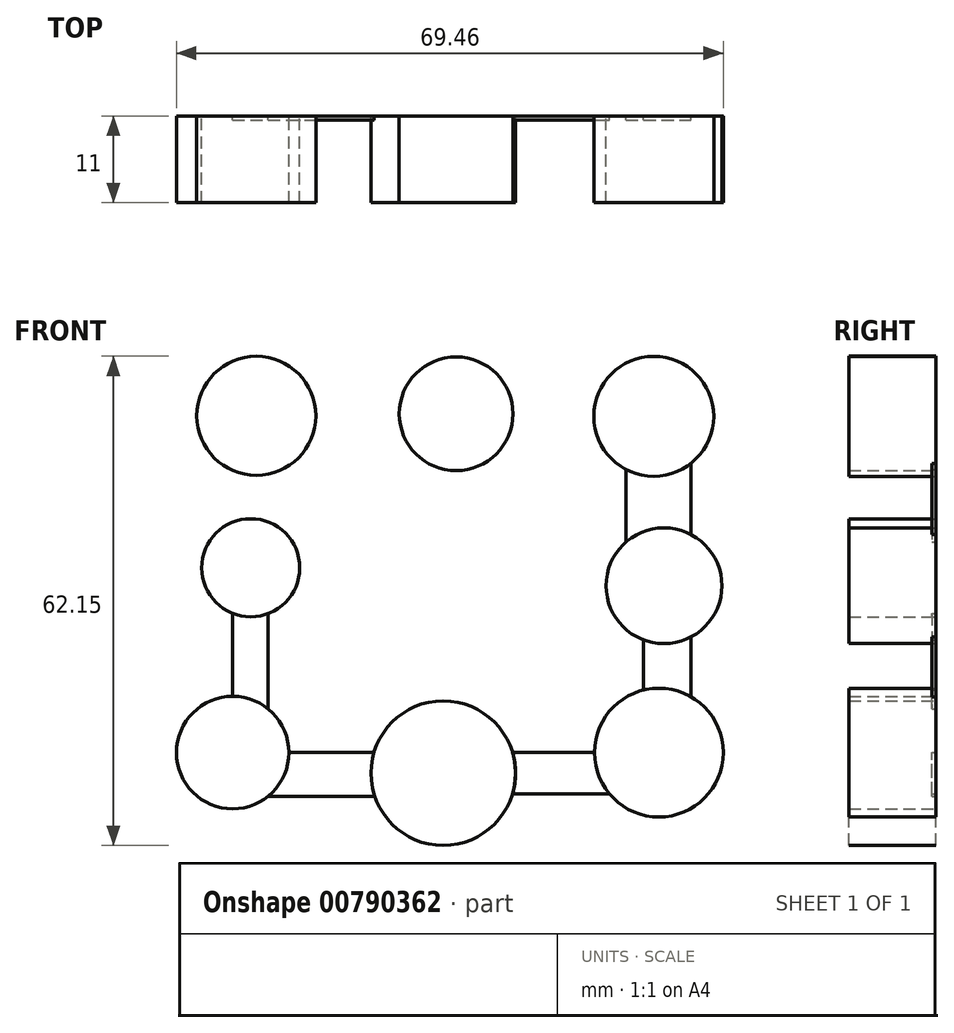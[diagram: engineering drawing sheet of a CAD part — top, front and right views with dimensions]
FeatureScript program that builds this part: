
annotation { "Feature Type Name" : "Feature", "Feature Type Description" : "" }
export const myFeature = defineFeature(function(context is Context, id is Id, definition is map)
    precondition{}
    {
        {
            var Q0;
            Q0=qCreatedBy(makeId("Front.planeOp"),FACE);
            var sketch = newSketch(context, id + "F0", { "sketchPlane" : qUnion([Q0])});
            skCircle(sketch, "E0", {"center": v(-55.2, 42.79) * mm, "radius": 7.57 * mm});
            skLineSegment(sketch, "E1", {"start": v(-48.07, 45.33) * mm, "end": v(-36.68, 45.33) * mm});
            skLineSegment(sketch, "E2", {"start": v(-48.08, 40.23) * mm, "end": v(-37, 40.23) * mm});
            skCircle(sketch, "E3", {"center": v(-29.83, 43.04) * mm, "radius": 7.22 * mm});
            skLineSegment(sketch, "E4", {"start": v(-23.46, 46.43) * mm, "end": v(-11.57, 46.43) * mm});
            skLineSegment(sketch, "E5", {"start": v(-23.31, 39.94) * mm, "end": v(-11.9, 39.94) * mm});
            skCircle(sketch, "E6", {"center": v(-4.72, 42.72) * mm, "radius": 7.61 * mm});
            skLineSegment(sketch, "E7", {"start": v(-58.22, 35.84) * mm, "end": v(-58.22, 29.35) * mm});
            skLineSegment(sketch, "E8", {"start": v(-52.3, 35.8) * mm, "end": v(-52.3, 28.7) * mm});
            skCircle(sketch, "E9", {"center": v(-55.92, 23.48) * mm, "radius": 6.23 * mm});
            skLineSegment(sketch, "E10", {"start": v(-58.22, 17.69) * mm, "end": v(-58.22, 6.2) * mm});
            skLineSegment(sketch, "E11", {"start": v(-53.72, 17.65) * mm, "end": v(-53.72, 5.54) * mm});
            skCircle(sketch, "E12", {"center": v(-58.22, 0) * mm, "radius": 7.14 * mm});
            skPoint(sketch, "E12.centerSnap0", {"position": v(-58.22, 11.94) * mm});
            skLineSegment(sketch, "E13", {"start": v(-51.08, 0) * mm, "end": v(-40.27, 0) * mm});
            skLineSegment(sketch, "E14", {"start": v(-53.72, -5.54) * mm, "end": v(-38.97, -5.54) * mm});
            skPoint(sketch, "E14.startSnap0", {"position": v(-53.72, 11.6) * mm});
            skCircle(sketch, "E15", {"center": v(-31.47, -2.6) * mm, "radius": 9.18 * mm});
            skLineSegment(sketch, "E16", {"start": v(-8.26, 35.97) * mm, "end": v(-8.26, 26.74) * mm});
            skLineSegment(sketch, "E17", {"start": v(0, 36.75) * mm, "end": v(0, 26.74) * mm});
            skCircle(sketch, "E18", {"center": v(-3.42, 21.2) * mm, "radius": 7.36 * mm});
            skCircle(sketch, "E19", {"center": v(-4.08, 0) * mm, "radius": 8.18 * mm});
            skLineSegment(sketch, "E20", {"start": v(-6.04, 14.32) * mm, "end": v(-6.04, 7.94) * mm});
            skLineSegment(sketch, "E21", {"start": v(0, 14.69) * mm, "end": v(0, 7.1) * mm});
            skLineSegment(sketch, "E22", {"start": v(-22.66, 0) * mm, "end": v(-12.25, 0) * mm});
            skLineSegment(sketch, "E23", {"start": v(-22.66, -5.22) * mm, "end": v(-10.37, -5.22) * mm});
            skSolve(sketch);
        }
        {
            var Q0;
            Q0=makeQuery(id+"F0.imprint","IMPRINT",FACE,{"disambiguationData":[TD([[makeQuery(id+"F0.imprint","IMPRINT",EDGE,{"derivedFrom":sQuery(id+"F0.wireOp",EDGE,"E0")}),1.0]])]});
            extrude(context, id + "F1", {"entities" : qUnion([Q0]), "depth" : 11 * mm, "offsetDistance" : 25.4 * mm});
        }
        {
            var Q0;
            {var subQ0=sQuery(id+"F0.wireOp",EDGE,"E9");var subQ1=makeQuery(id+"F0.imprint","INTERSECT",VERTEX,{"derivedFrom":[subQ0,sQuery(id+"F0.wireOp",EDGE,"E10")]});Q0=makeQuery(id+"F0.imprint","IMPRINT",FACE,{"disambiguationData":[TD([[makeQuery(id+"F0.imprint","IMPRINT",EDGE,{"disambiguationData":[TD([[subQ1,-1.0]])],"derivedFrom":subQ0}),1.0]])]});}
            var Q1;
            {var subQ0=sQuery(id+"F0.wireOp",EDGE,"E12");var subQ1=makeQuery(id+"F0.imprint","INTERSECT",VERTEX,{"derivedFrom":[sQuery(id+"F0.wireOp",EDGE,"E11"),subQ0]});Q1=makeQuery(id+"F0.imprint","IMPRINT",FACE,{"disambiguationData":[TD([[makeQuery(id+"F0.imprint","IMPRINT",EDGE,{"disambiguationData":[TD([[subQ1,1.0]])],"derivedFrom":subQ0}),1.0]])]});}
            var Q2;
            {var subQ0=sQuery(id+"F0.wireOp",EDGE,"E15");var subQ1=makeQuery(id+"F0.imprint","INTERSECT",VERTEX,{"derivedFrom":[sQuery(id+"F0.wireOp",EDGE,"E13"),subQ0]});Q2=makeQuery(id+"F0.imprint","IMPRINT",FACE,{"disambiguationData":[TD([[makeQuery(id+"F0.imprint","IMPRINT",EDGE,{"disambiguationData":[TD([[subQ1,1.0]])],"derivedFrom":subQ0}),1.0]])]});}
            var Q3;
            {var subQ0=sQuery(id+"F0.wireOp",EDGE,"E19");var subQ1=makeQuery(id+"F0.imprint","INTERSECT",VERTEX,{"derivedFrom":[subQ0,sQuery(id+"F0.wireOp",EDGE,"E20")]});Q3=makeQuery(id+"F0.imprint","IMPRINT",FACE,{"disambiguationData":[TD([[makeQuery(id+"F0.imprint","IMPRINT",EDGE,{"disambiguationData":[TD([[subQ1,1.0]])],"derivedFrom":subQ0}),1.0]])]});}
            var Q4;
            {var subQ0=sQuery(id+"F0.wireOp",EDGE,"E18");var subQ1=makeQuery(id+"F0.imprint","INTERSECT",VERTEX,{"derivedFrom":[sQuery(id+"F0.wireOp",EDGE,"E16"),subQ0]});Q4=makeQuery(id+"F0.imprint","IMPRINT",FACE,{"disambiguationData":[TD([[makeQuery(id+"F0.imprint","IMPRINT",EDGE,{"disambiguationData":[TD([[subQ1,1.0]])],"derivedFrom":subQ0}),1.0]])]});}
            var Q5;
            {var subQ0=sQuery(id+"F0.wireOp",EDGE,"E6");var subQ1=makeQuery(id+"F0.imprint","INTERSECT",VERTEX,{"derivedFrom":[subQ0,sQuery(id+"F0.wireOp",EDGE,"E16")]});Q5=makeQuery(id+"F0.imprint","IMPRINT",FACE,{"disambiguationData":[TD([[makeQuery(id+"F0.imprint","IMPRINT",EDGE,{"disambiguationData":[TD([[subQ1,-1.0]])],"derivedFrom":subQ0}),1.0]])]});}
            var Q6;
            {var subQ0=sQuery(id+"F0.wireOp",EDGE,"E3");var subQ1=makeQuery(id+"F0.imprint","IMPRINT",VERTEX,{"disambiguationData":[OD(0.0)],"derivedFrom":subQ0});Q6=makeQuery(id+"F0.imprint","IMPRINT",FACE,{"disambiguationData":[TD([[makeQuery(id+"F0.imprint","IMPRINT",EDGE,{"disambiguationData":[TD([[subQ1,1.0]])],"derivedFrom":subQ0}),1.0]])]});}
            extrude(context, id + "F2", {"entities" : qUnion([Q0, Q1, Q2, Q3, Q4, Q5, Q6]), "depth" : 11 * mm, "offsetDistance" : 25 * mm});
        }
        {
            var Q0;
            {var subQ0=sQuery(id+"F0.wireOp",EDGE,"E13");Q0=makeQuery(id+"F0.imprint","IMPRINT",FACE,{"disambiguationData":[TD([[makeQuery(id+"F0.imprint","IMPRINT",EDGE,{"derivedFrom":subQ0}),-1.0]])]});}
            var Q1;
            {var subQ0=sQuery(id+"F0.wireOp",EDGE,"E22");Q1=makeQuery(id+"F0.imprint","IMPRINT",FACE,{"disambiguationData":[TD([[makeQuery(id+"F0.imprint","IMPRINT",EDGE,{"derivedFrom":subQ0}),-1.0]])]});}
            var Q2;
            {var subQ0=sQuery(id+"F0.wireOp",EDGE,"E20");Q2=makeQuery(id+"F0.imprint","IMPRINT",FACE,{"disambiguationData":[TD([[makeQuery(id+"F0.imprint","IMPRINT",EDGE,{"derivedFrom":subQ0}),1.0]])]});}
            var Q3;
            {var subQ0=sQuery(id+"F0.wireOp",EDGE,"E16");Q3=makeQuery(id+"F0.imprint","IMPRINT",FACE,{"disambiguationData":[TD([[makeQuery(id+"F0.imprint","IMPRINT",EDGE,{"derivedFrom":subQ0}),1.0]])]});}
            var Q4;
            {var subQ3=sQuery(id+"F0.wireOp",EDGE,"E11");Q4=makeQuery(id+"F0.imprint","IMPRINT",FACE,{"disambiguationData":[TD([[makeQuery(id+"F0.imprint","IMPRINT",EDGE,{"derivedFrom":subQ3}),-1.0]])]});}
            extrude(context, id + "F3", {"entities" : qUnion([Q0, Q1, Q2, Q3, Q4]), "depth" : 0.5 * mm, "offsetDistance" : 25 * mm});
        }
        {
            var Q0;
            Q0=sQuery(id+"F0.wireOp",EDGE,"E8");
            var Q1;
            Q1=sQuery(id+"F0.wireOp",EDGE,"E7");
            var Q2;
            Q2=sQuery(id+"F0.wireOp",EDGE,"E5");
            var Q3;
            Q3=sQuery(id+"F0.wireOp",EDGE,"E2");
            var Q4;
            Q4=sQuery(id+"F0.wireOp",EDGE,"E1");
            var Q5;
            Q5=sQuery(id+"F0.wireOp",EDGE,"E4");
            extrude(context, id + "F4", {"bodyType" : ToolBodyType.SURFACE, "surfaceEntities" : qUnion([Q0, Q1, Q2, Q3, Q4, Q5]), "depth" : 1 * mm, "offsetDistance" : 25 * mm});
        }
    });
